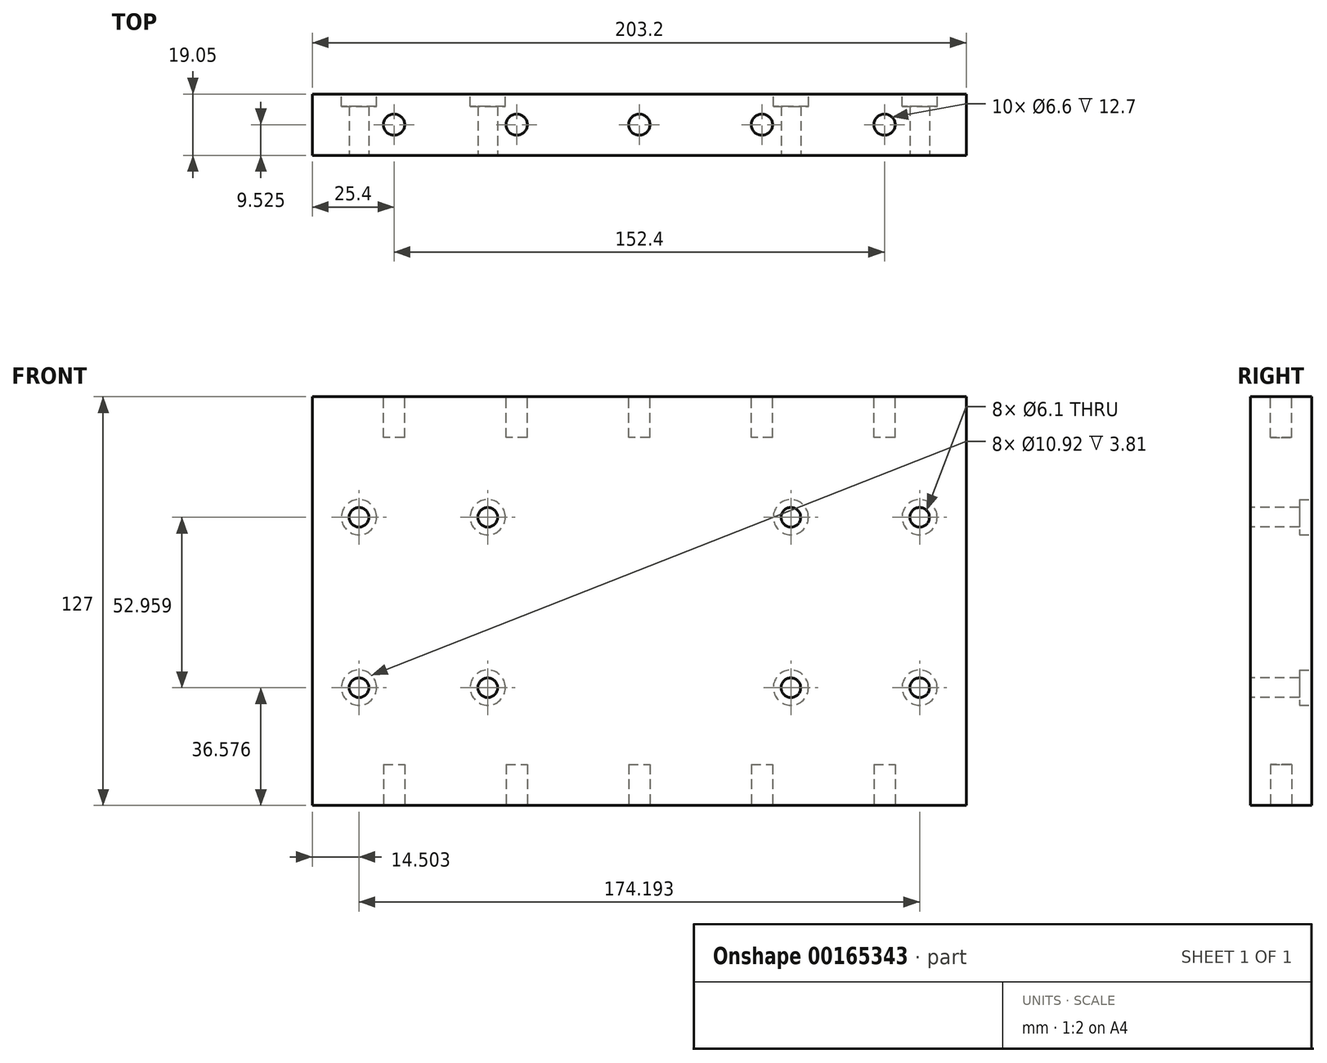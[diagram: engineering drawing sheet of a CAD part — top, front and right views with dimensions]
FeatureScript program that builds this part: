
annotation { "Feature Type Name" : "Feature", "Feature Type Description" : "" }
export const myFeature = defineFeature(function(context is Context, id is Id, definition is map)
    precondition{}
    {
        {
            var Q0;
            Q0=qCreatedBy(makeId("Front.planeOp"),FACE);
            var sketch = newSketch(context, id + "F0", { "sketchPlane" : qUnion([Q0])});
            skLineSegment(sketch, "E0.rect.bottom", {"start": v(101.6, 63.5) * mm, "end": v(-101.6, 63.5) * mm});
            skLineSegment(sketch, "E0.rect.top", {"start": v(101.6, -63.5) * mm, "end": v(-101.6, -63.5) * mm});
            skLineSegment(sketch, "E0.rect.left", {"start": v(101.6, 63.5) * mm, "end": v(101.6, -63.5) * mm});
            skLineSegment(sketch, "E0.rect.right", {"start": v(-101.6, 63.5) * mm, "end": v(-101.6, -63.5) * mm});
            skPoint(sketch, "E0.rect.middle", {"position": v(0, 0) * mm});
            skSolve(sketch);
        }
        {
            var Q0;
            Q0=qSketchRegion(id+"F0",true);
            extrude(context, id + "F1", {"entities" : qUnion([Q0]), "depth" : 19.05 * mm});
        }
        {
            var Q0;
            Q0=makeQuery(id+"F1.opExtrude","CAP_FACE",FACE,{"disambiguationData":[OSD([sQuery(id+"F0.wireOp",EDGE,"E0.rect.bottom"),sQuery(id+"F0.wireOp",EDGE,"E0.rect.top"),sQuery(id+"F0.wireOp",EDGE,"E0.rect.left"),sQuery(id+"F0.wireOp",EDGE,"E0.rect.right")])],"isStart":false});
            var sketch = newSketch(context, id + "F2", { "sketchPlane" : qUnion([Q0])});
            skLineSegment(sketch, "E1", {"start": v(-87.1, 63.5) * mm, "end": v(-87.1, -63.5) * mm, "construction": true});
            skLineSegment(sketch, "E2", {"start": v(-47.1, 63.5) * mm, "end": v(-47.1, -63.5) * mm, "construction": true});
            skLineSegment(sketch, "E3", {"start": v(47.1, 63.5) * mm, "end": v(47.1, -63.5) * mm, "construction": true});
            skLineSegment(sketch, "E4", {"start": v(47.1, -63.5) * mm, "end": v(48.06, -63.46) * mm, "construction": true});
            skLineSegment(sketch, "E5", {"start": v(87.1, 63.5) * mm, "end": v(87.1, -63.46) * mm, "construction": true});
            skLineSegment(sketch, "E6", {"start": v(-101.6, 26.03) * mm, "end": v(101.6, 26.04) * mm, "construction": true});
            skLineSegment(sketch, "E7", {"start": v(-101.6, -26.92) * mm, "end": v(101.6, -26.92) * mm, "construction": true});
            skCircle(sketch, "E8", {"center": v(-87.1, 26.03) * mm, "radius": 3.05 * mm});
            skCircle(sketch, "E9", {"center": v(-47.1, 26.03) * mm, "radius": 3.05 * mm});
            skCircle(sketch, "E10", {"center": v(-87.1, -26.92) * mm, "radius": 3.05 * mm});
            skCircle(sketch, "E11", {"center": v(-47.1, -26.92) * mm, "radius": 3.05 * mm});
            skCircle(sketch, "E12", {"center": v(47.1, -26.92) * mm, "radius": 3.05 * mm});
            skCircle(sketch, "E13", {"center": v(47.1, 26.04) * mm, "radius": 3.05 * mm});
            skCircle(sketch, "E14", {"center": v(87.1, 26.04) * mm, "radius": 3.05 * mm});
            skCircle(sketch, "E15", {"center": v(87.1, -26.92) * mm, "radius": 3.05 * mm});
            skLineSegment(sketch, "E16", {"start": v(101.6, 0) * mm, "end": v(-101.6, 0) * mm, "construction": true});
            skSolve(sketch);
        }
        {
            var Q0;
            Q0=qSketchRegion(id+"F2",true);
            extrude(context, id + "F3", {"entities" : qUnion([Q0]), "operationType" : NewBodyOperationType.REMOVE, "endBound" : BoundingType.THROUGH_ALL, "oppositeDirection" : true, "depth" : 25.4 * mm});
        }
        {
            var Q0;
            Q0=makeQuery(id+"F1.opExtrude","SWEPT_FACE",FACE,{"disambiguationData":[OSD([sQuery(id+"F0.wireOp",EDGE,"E0.rect.bottom")])]});
            var sketch = newSketch(context, id + "F4", { "sketchPlane" : qUnion([Q0])});
            skLineSegment(sketch, "E17", {"start": v(-101.6, -9.53) * mm, "end": v(101.6, -9.53) * mm, "construction": true});
            skLineSegment(sketch, "E18", {"start": v(-76.2, 0) * mm, "end": v(-76.2, -19.05) * mm, "construction": true});
            skLineSegment(sketch, "E19", {"start": v(-38.1, 0) * mm, "end": v(-38.1, -19.05) * mm, "construction": true});
            skLineSegment(sketch, "E20", {"start": v(0, 0) * mm, "end": v(0, -19.05) * mm, "construction": true});
            skLineSegment(sketch, "E21", {"start": v(38.1, 0) * mm, "end": v(38.1, -19.05) * mm, "construction": true});
            skLineSegment(sketch, "E22", {"start": v(76.2, 0) * mm, "end": v(76.2, -19.05) * mm, "construction": true});
            skCircle(sketch, "E23", {"center": v(-76.2, -9.53) * mm, "radius": 3.3 * mm});
            skCircle(sketch, "E24", {"center": v(-38.1, -9.53) * mm, "radius": 3.3 * mm});
            skCircle(sketch, "E25", {"center": v(0, -9.53) * mm, "radius": 3.3 * mm});
            skCircle(sketch, "E26", {"center": v(38.1, -9.52) * mm, "radius": 3.3 * mm});
            skCircle(sketch, "E27", {"center": v(76.2, -9.52) * mm, "radius": 3.3 * mm});
            skSolve(sketch);
        }
        {
            var Q0;
            Q0=qSketchRegion(id+"F4",true);
            extrude(context, id + "F5", {"entities" : qUnion([Q0]), "operationType" : NewBodyOperationType.REMOVE, "oppositeDirection" : true, "depth" : 12.7 * mm});
        }
        {
            var Q0;
            Q0=makeQuery(id+"F1.opExtrude","SWEPT_FACE",FACE,{"disambiguationData":[OSD([sQuery(id+"F0.wireOp",EDGE,"E0.rect.top")])]});
            var sketch = newSketch(context, id + "F6", { "sketchPlane" : qUnion([Q0])});
            skSolve(sketch);
        }
        {
            var Q0;
            {var subQ0=sQuery(id+"F0.wireOp",EDGE,"E0.rect.top");Q0=makeQuery(id+"F6.imprint","IMPRINT",FACE,{"disambiguationData":[TD([[makeQuery(id+"F6.imprint","IMPRINT",EDGE,{"derivedFrom":makeQuery(id+"F1.opExtrude","CAP_EDGE",EDGE,{"disambiguationData":[OSD([subQ0])],"isStart":true})}),-1.0]])]});}
            var sketch = newSketch(context, id + "F7", { "sketchPlane" : qUnion([Q0])});
            skLineSegment(sketch, "E28", {"start": v(77.9, 9.53) * mm, "end": v(-77.9, 9.52) * mm, "construction": true});
            skLineSegment(sketch, "E29", {"start": v(-76.2, 14.67) * mm, "end": v(-76.2, 0) * mm, "construction": true});
            skLineSegment(sketch, "E30", {"start": v(-38.1, 14.77) * mm, "end": v(-38.1, 0) * mm, "construction": true});
            skLineSegment(sketch, "E31", {"start": v(-38.1, 0) * mm, "end": v(-38.3, -0.45) * mm, "construction": true});
            skLineSegment(sketch, "E32", {"start": v(0, 14.67) * mm, "end": v(0, 0) * mm, "construction": true});
            skLineSegment(sketch, "E33", {"start": v(38.1, 14.67) * mm, "end": v(38.1, 0) * mm, "construction": true});
            skLineSegment(sketch, "E34", {"start": v(76.2, 14.67) * mm, "end": v(76.2, 0) * mm, "construction": true});
            skCircle(sketch, "E35", {"center": v(-76.2, 9.52) * mm, "radius": 3.3 * mm});
            skCircle(sketch, "E36", {"center": v(-38.1, 9.52) * mm, "radius": 3.3 * mm});
            skCircle(sketch, "E37", {"center": v(0, 9.53) * mm, "radius": 3.3 * mm});
            skCircle(sketch, "E38", {"center": v(38.1, 9.53) * mm, "radius": 3.3 * mm});
            skCircle(sketch, "E39", {"center": v(76.2, 9.53) * mm, "radius": 3.3 * mm});
            skSolve(sketch);
        }
        {
            var Q0;
            Q0=qSketchRegion(id+"F7",true);
            extrude(context, id + "F8", {"entities" : qUnion([Q0]), "operationType" : NewBodyOperationType.REMOVE, "oppositeDirection" : true, "depth" : 12.7 * mm});
        }
        {
            var Q0;
            Q0=makeQuery(id+"F1.opExtrude","CAP_FACE",FACE,{"disambiguationData":[OSD([sQuery(id+"F0.wireOp",EDGE,"E0.rect.bottom"),sQuery(id+"F0.wireOp",EDGE,"E0.rect.top"),sQuery(id+"F0.wireOp",EDGE,"E0.rect.left"),sQuery(id+"F0.wireOp",EDGE,"E0.rect.right")])],"isStart":true});
            var sketch = newSketch(context, id + "F9", { "sketchPlane" : qUnion([Q0])});
            skCircle(sketch, "E40", {"center": v(-47.1, 26.04) * mm, "radius": 5.46 * mm});
            skCircle(sketch, "E41", {"center": v(-87.1, 26.04) * mm, "radius": 5.46 * mm});
            skCircle(sketch, "E42", {"center": v(-87.1, -26.92) * mm, "radius": 5.46 * mm});
            skCircle(sketch, "E43", {"center": v(-47.1, -26.92) * mm, "radius": 5.46 * mm});
            skCircle(sketch, "E44", {"center": v(47.1, -26.92) * mm, "radius": 5.46 * mm});
            skCircle(sketch, "E45", {"center": v(87.1, -26.92) * mm, "radius": 5.46 * mm});
            skCircle(sketch, "E46", {"center": v(87.1, 26.03) * mm, "radius": 5.46 * mm});
            skCircle(sketch, "E47", {"center": v(47.1, 26.03) * mm, "radius": 5.46 * mm});
            skSolve(sketch);
        }
        {
            var Q0;
            Q0=qSketchRegion(id+"F9",true);
            extrude(context, id + "F10", {"entities" : qUnion([Q0]), "operationType" : NewBodyOperationType.REMOVE, "oppositeDirection" : true, "depth" : 3.8 * mm});
        }
    });
